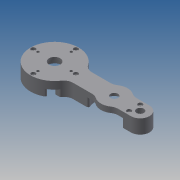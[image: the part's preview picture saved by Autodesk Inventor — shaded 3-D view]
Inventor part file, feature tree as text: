
AUTODESK INVENTOR PART (.ipt)
format: ipt  version: 2013 (Build 170138000, 138)  size: 354,816 bytes
history: native  units: mm
features: extrude x20, sketch x20, fillet x2, projected_geometry x2, mirror x1, pattern_circular x1
ambient origin geometry x8: Origin, YZ Plane, XZ Plane, XY Plane, X Axis, Y Axis, Z Axis, Center Point
bodies: Solid1 (feature_tree)
feature tree (46):
  extrude  "Extrusion1"  Depth=12.5mm
  extrude  "Extrusion2"  Depth=38.0mm TaperAngle=0.0deg
  extrude  "Extrusion3"  Depth=35.0mm
  extrude  "Extrusion4"  Depth=35.0mm TaperAngle=0.0deg
  extrude  "Extrusion5"  Depth=23.0mm TaperAngle=0.0deg
  mirror  "Mirror1"
  extrude  "Extrusion6"  Depth=4.0mm TaperAngle=0.0deg
  extrude  "Extrusion7"  Depth=4.0mm TaperAngle=0.0deg
  extrude  "Extrusion9"  Depth=7.5mm
  extrude  "Extrusion10"  Depth=7.5mm
  extrude  "Extrusion11"  Depth=3.0mm TaperAngle=0.0deg
  extrude  "Extrusion12"  Depth=3.0mm TaperAngle=0.0deg
  extrude  "Extrusion13"  Depth=1.5mm TaperAngle=0.0deg
  extrude  "Extrusion14"  Depth=65.0mm
  extrude  "Extrusion15"  Depth=1.5mm TaperAngle=0.0deg
  extrude  "Extrusion16"  Depth=11.4mm TaperAngle=0.0deg
  extrude  "Extrusion17"  Depth=15.0mm
  extrude  "Extrusion18"  Depth=22.0mm
  extrude  "Extrusion19"  Depth=44.055422mm
  pattern_circular  "Circular Pattern2"  [2 undecoded]
  extrude  "Extrusion20"  Depth=3.5mm
  fillet  "Fillet1"  Radius=7.0mm
  fillet  "Fillet2"  Radius=5.5mm
  extrude  "Extrusion21"  Depth=4.0mm TaperAngle=0.0deg
  sketch  "Sketch1"  dims[d0=115.5mm d2=12.5mm]
  sketch  "Sketch2"  dims[d3=12.0mm d4=38.0mm d5=0.0mm]
  sketch  "Sketch3"  dims[d6=44.563422mm d8=35.0mm]
  sketch  "Sketch4"  dims[d9=10.0mm d10=35.0mm d11=0.0mm]
  sketch  "Sketch5"  dims[d12=50.0mm d14=23.0mm d15=0.0mm]
  sketch  "Sketch6"  dims[d16=21.0mm d19=4.0mm d20=0.0mm]
  projected_geometry  "Projected Loop1"
  sketch  "Sketch7"  dims[d22=7.5mm d23=4.0mm d24=0.0mm]
  sketch  "Sketch9"  dims[d25=3.0mm d27=7.5mm]
  sketch  "Sketch10"  dims[d28=7.5mm d29=7.5mm]
  sketch  "Sketch11"  dims[d30=7.5mm d31=3.0mm d32=0.0mm]
  sketch  "Sketch12"  dims[d33=6.0mm d36=3.0mm d37=0.0mm]
  sketch  "Sketch13"  dims[d43=1.0mm d44=1.5mm d45=0.0mm]
  sketch  "Sketch14"  dims[d46=1.5mm d47=0.0mm d50=65.0mm]
  sketch  "Sketch15"  dims[d51=7.5mm d52=1.5mm d53=0.0mm]
  sketch  "Sketch16"  dims[d54=1.5mm d55=0.0mm d56=11.4mm d57=0.0mm]
  sketch  "Sketch17"  dims[d58=5.0mm d59=0.0mm d60=15.0mm]
  sketch  "Sketch18"  dims[d62=5.0mm d63=0.0mm d64=22.0mm]
  sketch  "Sketch19"  dims[d66=7.0mm d67=0.0mm d68=44.055422mm]
  sketch  "Sketch20"  dims[d71=7.0mm d72=0.0mm]
  sketch  "Sketch21"  dims[d73=28.75mm d74=22.5mm d75=3.5mm d76=7.0mm d77=0.0mm d78=5.5mm d79=4.0mm d80=100.0mm d81=0.0mm d82=0.0mm d83=40.0mm d84=360.0deg d86=6.0mm d88=3.0mm d89=0.0mm d90=2.0mm d91=12.5mm d92=1.0mm d93=1.0mm d94=0.0mm]
  projected_geometry  "Project Cut Edges1"
note: 2 required parameter values undecoded (feature->parameter linkage not recoverable at this tier; creation-order binding heuristic only, values carry confidence <= 0.55)
